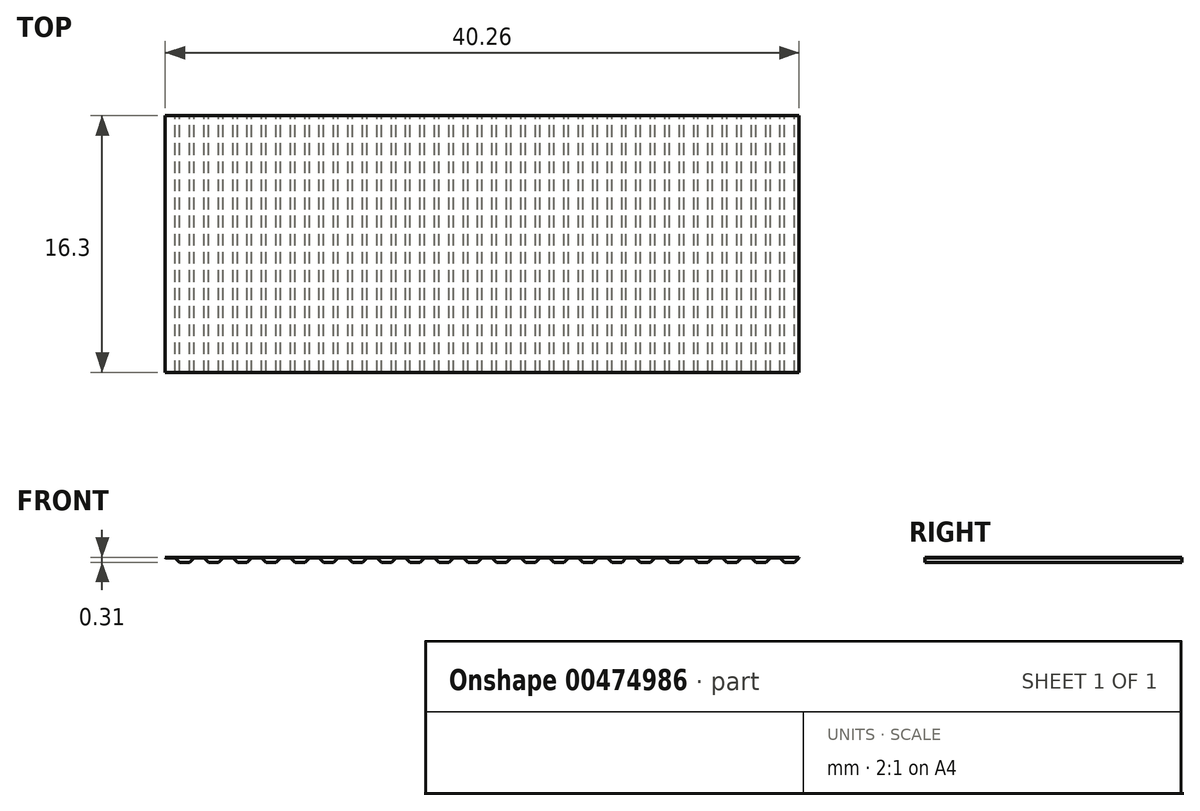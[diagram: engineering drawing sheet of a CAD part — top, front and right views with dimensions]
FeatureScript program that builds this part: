
annotation { "Feature Type Name" : "Feature", "Feature Type Description" : "" }
export const myFeature = defineFeature(function(context is Context, id is Id, definition is map)
    precondition{}
    {
        {
            var Q0;
            Q0=qCreatedBy(makeId("Front.planeOp"),FACE);
            var sketch = newSketch(context, id + "F0", { "sketchPlane" : qUnion([Q0])});
            skLineSegment(sketch, "E0", {"start": v(-5.24, 1) * mm, "end": v(-3.4, 1) * mm});
            skLineSegment(sketch, "E1", {"start": v(-5.23, 0.95) * mm, "end": v(-4.6, 0.95) * mm});
            skLineSegment(sketch, "E2", {"start": v(-4.6, 0.95) * mm, "end": v(-4.32, 0.68) * mm});
            skLineSegment(sketch, "E3", {"start": v(-4.32, 0.68) * mm, "end": v(-3.69, 0.68) * mm});
            skLineSegment(sketch, "E4", {"start": v(-3.69, 0.68) * mm, "end": v(-3.4, 0.95) * mm});
            skLineSegment(sketch, "E5", {"start": v(-5.24, 1) * mm, "end": v(-5.23, 0.95) * mm});
            skLineSegment(sketch, "E6", {"start": v(-3.4, 1) * mm, "end": v(-3.4, 0.95) * mm});
            skLineSegment(sketch, "E7", {"start": v(-3.4, 1) * mm, "end": v(-1.57, 1) * mm});
            skLineSegment(sketch, "E8", {"start": v(-3.4, 0.95) * mm, "end": v(-2.77, 0.95) * mm});
            skLineSegment(sketch, "E9", {"start": v(-2.77, 0.95) * mm, "end": v(-2.49, 0.68) * mm});
            skLineSegment(sketch, "E10", {"start": v(-2.49, 0.68) * mm, "end": v(-1.86, 0.68) * mm});
            skLineSegment(sketch, "E11", {"start": v(-1.86, 0.68) * mm, "end": v(-1.57, 0.95) * mm});
            skLineSegment(sketch, "E12", {"start": v(-1.57, 1) * mm, "end": v(-1.57, 0.95) * mm});
            skLineSegment(sketch, "E13", {"start": v(-1.58, 1) * mm, "end": v(0.26, 1) * mm});
            skLineSegment(sketch, "E14", {"start": v(-1.57, 0.95) * mm, "end": v(-0.94, 0.95) * mm});
            skLineSegment(sketch, "E15", {"start": v(-0.94, 0.95) * mm, "end": v(-0.66, 0.68) * mm});
            skLineSegment(sketch, "E16", {"start": v(-0.66, 0.68) * mm, "end": v(-0.03, 0.68) * mm});
            skLineSegment(sketch, "E17", {"start": v(-0.03, 0.68) * mm, "end": v(0.26, 0.95) * mm});
            skLineSegment(sketch, "E18", {"start": v(-1.58, 1) * mm, "end": v(-1.57, 0.95) * mm});
            skLineSegment(sketch, "E19", {"start": v(0.26, 1) * mm, "end": v(0.26, 0.95) * mm});
            skLineSegment(sketch, "E20", {"start": v(0.25, 1) * mm, "end": v(2.09, 1) * mm});
            skLineSegment(sketch, "E21", {"start": v(0.26, 0.95) * mm, "end": v(0.89, 0.95) * mm});
            skLineSegment(sketch, "E22", {"start": v(0.89, 0.95) * mm, "end": v(1.17, 0.68) * mm});
            skLineSegment(sketch, "E23", {"start": v(1.17, 0.68) * mm, "end": v(1.8, 0.68) * mm});
            skLineSegment(sketch, "E24", {"start": v(1.8, 0.68) * mm, "end": v(2.09, 0.95) * mm});
            skLineSegment(sketch, "E25", {"start": v(0.25, 1) * mm, "end": v(0.26, 0.95) * mm});
            skLineSegment(sketch, "E26", {"start": v(2.09, 1) * mm, "end": v(2.09, 0.95) * mm});
            skLineSegment(sketch, "E27", {"start": v(2.08, 1) * mm, "end": v(3.92, 1) * mm});
            skLineSegment(sketch, "E28", {"start": v(2.09, 0.95) * mm, "end": v(2.72, 0.95) * mm});
            skLineSegment(sketch, "E29", {"start": v(2.72, 0.95) * mm, "end": v(3, 0.68) * mm});
            skLineSegment(sketch, "E30", {"start": v(3, 0.68) * mm, "end": v(3.63, 0.68) * mm});
            skLineSegment(sketch, "E31", {"start": v(3.63, 0.68) * mm, "end": v(3.92, 0.95) * mm});
            skLineSegment(sketch, "E32", {"start": v(2.08, 1) * mm, "end": v(2.09, 0.95) * mm});
            skLineSegment(sketch, "E33", {"start": v(3.92, 1) * mm, "end": v(3.92, 0.95) * mm});
            skLineSegment(sketch, "E34", {"start": v(3.91, 1) * mm, "end": v(5.75, 1) * mm});
            skLineSegment(sketch, "E35", {"start": v(3.92, 0.95) * mm, "end": v(4.55, 0.95) * mm});
            skLineSegment(sketch, "E36", {"start": v(4.55, 0.95) * mm, "end": v(4.83, 0.68) * mm});
            skLineSegment(sketch, "E37", {"start": v(4.83, 0.68) * mm, "end": v(5.46, 0.68) * mm});
            skLineSegment(sketch, "E38", {"start": v(5.46, 0.68) * mm, "end": v(5.74, 0.95) * mm});
            skLineSegment(sketch, "E39", {"start": v(3.91, 1) * mm, "end": v(3.92, 0.95) * mm});
            skLineSegment(sketch, "E40", {"start": v(5.75, 1) * mm, "end": v(5.74, 0.95) * mm});
            skLineSegment(sketch, "E41", {"start": v(5.74, 1) * mm, "end": v(7.58, 1) * mm});
            skLineSegment(sketch, "E42", {"start": v(5.74, 0.95) * mm, "end": v(6.37, 0.95) * mm});
            skLineSegment(sketch, "E43", {"start": v(6.37, 0.95) * mm, "end": v(6.66, 0.68) * mm});
            skLineSegment(sketch, "E44", {"start": v(6.66, 0.68) * mm, "end": v(7.29, 0.68) * mm});
            skLineSegment(sketch, "E45", {"start": v(7.29, 0.68) * mm, "end": v(7.57, 0.95) * mm});
            skLineSegment(sketch, "E46", {"start": v(5.74, 1) * mm, "end": v(5.74, 0.95) * mm});
            skLineSegment(sketch, "E47", {"start": v(7.58, 1) * mm, "end": v(7.57, 0.95) * mm});
            skLineSegment(sketch, "E48", {"start": v(7.57, 1) * mm, "end": v(9.4, 1) * mm});
            skLineSegment(sketch, "E49", {"start": v(7.57, 0.95) * mm, "end": v(8.2, 0.95) * mm});
            skLineSegment(sketch, "E50", {"start": v(8.2, 0.95) * mm, "end": v(8.49, 0.68) * mm});
            skLineSegment(sketch, "E51", {"start": v(8.49, 0.68) * mm, "end": v(9.12, 0.68) * mm});
            skLineSegment(sketch, "E52", {"start": v(9.12, 0.68) * mm, "end": v(9.4, 0.95) * mm});
            skLineSegment(sketch, "E53", {"start": v(7.57, 1) * mm, "end": v(7.57, 0.95) * mm});
            skLineSegment(sketch, "E54", {"start": v(9.4, 1) * mm, "end": v(9.4, 0.95) * mm});
            skLineSegment(sketch, "E55", {"start": v(9.4, 1) * mm, "end": v(11.24, 1) * mm});
            skLineSegment(sketch, "E56", {"start": v(9.4, 0.95) * mm, "end": v(10.03, 0.95) * mm});
            skLineSegment(sketch, "E57", {"start": v(10.03, 0.95) * mm, "end": v(10.32, 0.68) * mm});
            skLineSegment(sketch, "E58", {"start": v(10.32, 0.68) * mm, "end": v(10.95, 0.68) * mm});
            skLineSegment(sketch, "E59", {"start": v(10.95, 0.68) * mm, "end": v(11.23, 0.95) * mm});
            skLineSegment(sketch, "E60", {"start": v(11.24, 1) * mm, "end": v(11.23, 0.95) * mm});
            skLineSegment(sketch, "E61", {"start": v(11.23, 1) * mm, "end": v(13.07, 1) * mm});
            skLineSegment(sketch, "E62", {"start": v(11.23, 0.95) * mm, "end": v(11.86, 0.95) * mm});
            skLineSegment(sketch, "E63", {"start": v(11.86, 0.95) * mm, "end": v(12.15, 0.68) * mm});
            skLineSegment(sketch, "E64", {"start": v(12.15, 0.68) * mm, "end": v(12.78, 0.68) * mm});
            skLineSegment(sketch, "E65", {"start": v(12.78, 0.68) * mm, "end": v(13.06, 0.95) * mm});
            skLineSegment(sketch, "E66", {"start": v(11.23, 1) * mm, "end": v(11.23, 0.95) * mm});
            skLineSegment(sketch, "E67", {"start": v(13.07, 1) * mm, "end": v(13.06, 0.95) * mm});
            skLineSegment(sketch, "E68", {"start": v(13.06, 1) * mm, "end": v(14.9, 1) * mm});
            skLineSegment(sketch, "E69", {"start": v(13.06, 0.95) * mm, "end": v(13.7, 0.95) * mm});
            skLineSegment(sketch, "E70", {"start": v(13.7, 0.95) * mm, "end": v(13.98, 0.68) * mm});
            skLineSegment(sketch, "E71", {"start": v(13.98, 0.68) * mm, "end": v(14.6, 0.68) * mm});
            skLineSegment(sketch, "E72", {"start": v(14.6, 0.68) * mm, "end": v(14.9, 0.95) * mm});
            skLineSegment(sketch, "E73", {"start": v(13.06, 1) * mm, "end": v(13.06, 0.95) * mm});
            skLineSegment(sketch, "E74", {"start": v(14.9, 1) * mm, "end": v(14.9, 0.95) * mm});
            skLineSegment(sketch, "E75", {"start": v(14.89, 1) * mm, "end": v(16.72, 1) * mm});
            skLineSegment(sketch, "E76", {"start": v(14.9, 0.95) * mm, "end": v(15.52, 0.95) * mm});
            skLineSegment(sketch, "E77", {"start": v(15.52, 0.95) * mm, "end": v(15.8, 0.68) * mm});
            skLineSegment(sketch, "E78", {"start": v(15.8, 0.68) * mm, "end": v(16.44, 0.68) * mm});
            skLineSegment(sketch, "E79", {"start": v(16.44, 0.68) * mm, "end": v(16.72, 0.95) * mm});
            skLineSegment(sketch, "E80", {"start": v(14.89, 1) * mm, "end": v(14.9, 0.95) * mm});
            skLineSegment(sketch, "E81", {"start": v(16.72, 1) * mm, "end": v(16.72, 0.95) * mm});
            skLineSegment(sketch, "E82", {"start": v(16.72, 1) * mm, "end": v(18.55, 1) * mm});
            skLineSegment(sketch, "E83", {"start": v(16.72, 0.95) * mm, "end": v(17.35, 0.95) * mm});
            skLineSegment(sketch, "E84", {"start": v(17.35, 0.95) * mm, "end": v(17.64, 0.68) * mm});
            skLineSegment(sketch, "E85", {"start": v(17.64, 0.68) * mm, "end": v(18.27, 0.68) * mm});
            skLineSegment(sketch, "E86", {"start": v(18.27, 0.68) * mm, "end": v(18.55, 0.95) * mm});
            skLineSegment(sketch, "E87", {"start": v(18.55, 1) * mm, "end": v(18.55, 0.95) * mm});
            skLineSegment(sketch, "E88", {"start": v(18.55, 1) * mm, "end": v(20.38, 1) * mm});
            skLineSegment(sketch, "E89", {"start": v(18.55, 0.95) * mm, "end": v(19.18, 0.95) * mm});
            skLineSegment(sketch, "E90", {"start": v(19.18, 0.95) * mm, "end": v(19.46, 0.68) * mm});
            skLineSegment(sketch, "E91", {"start": v(19.46, 0.68) * mm, "end": v(20.1, 0.68) * mm});
            skLineSegment(sketch, "E92", {"start": v(20.1, 0.68) * mm, "end": v(20.38, 0.95) * mm});
            skLineSegment(sketch, "E93", {"start": v(20.38, 1) * mm, "end": v(20.38, 0.95) * mm});
            skLineSegment(sketch, "E94", {"start": v(20.38, 1) * mm, "end": v(22.21, 1) * mm});
            skLineSegment(sketch, "E95", {"start": v(20.38, 0.95) * mm, "end": v(21, 0.95) * mm});
            skLineSegment(sketch, "E96", {"start": v(21, 0.95) * mm, "end": v(21.3, 0.68) * mm});
            skLineSegment(sketch, "E97", {"start": v(21.3, 0.68) * mm, "end": v(21.92, 0.68) * mm});
            skLineSegment(sketch, "E98", {"start": v(21.92, 0.68) * mm, "end": v(22.2, 0.95) * mm});
            skLineSegment(sketch, "E99", {"start": v(22.21, 1) * mm, "end": v(22.2, 0.95) * mm});
            skLineSegment(sketch, "E100", {"start": v(22.2, 1) * mm, "end": v(24.04, 1) * mm});
            skLineSegment(sketch, "E101", {"start": v(22.2, 0.95) * mm, "end": v(22.84, 0.95) * mm});
            skLineSegment(sketch, "E102", {"start": v(22.84, 0.95) * mm, "end": v(23.12, 0.68) * mm});
            skLineSegment(sketch, "E103", {"start": v(23.12, 0.68) * mm, "end": v(23.75, 0.68) * mm});
            skLineSegment(sketch, "E104", {"start": v(23.75, 0.68) * mm, "end": v(24.04, 0.95) * mm});
            skLineSegment(sketch, "E105", {"start": v(22.2, 1) * mm, "end": v(22.2, 0.95) * mm});
            skLineSegment(sketch, "E106", {"start": v(24.04, 1) * mm, "end": v(24.04, 0.95) * mm});
            skLineSegment(sketch, "E107", {"start": v(24.04, 1) * mm, "end": v(25.87, 1) * mm});
            skLineSegment(sketch, "E108", {"start": v(24.04, 0.95) * mm, "end": v(24.67, 0.95) * mm});
            skLineSegment(sketch, "E109", {"start": v(24.67, 0.95) * mm, "end": v(24.95, 0.68) * mm});
            skLineSegment(sketch, "E110", {"start": v(24.95, 0.68) * mm, "end": v(25.58, 0.68) * mm});
            skLineSegment(sketch, "E111", {"start": v(25.58, 0.68) * mm, "end": v(25.87, 0.95) * mm});
            skLineSegment(sketch, "E112", {"start": v(25.87, 1) * mm, "end": v(25.87, 0.95) * mm});
            skLineSegment(sketch, "E113", {"start": v(25.86, 1) * mm, "end": v(27.7, 1) * mm});
            skLineSegment(sketch, "E114", {"start": v(25.87, 0.95) * mm, "end": v(26.5, 0.95) * mm});
            skLineSegment(sketch, "E115", {"start": v(26.5, 0.95) * mm, "end": v(26.78, 0.68) * mm});
            skLineSegment(sketch, "E116", {"start": v(26.78, 0.68) * mm, "end": v(27.41, 0.68) * mm});
            skLineSegment(sketch, "E117", {"start": v(27.41, 0.68) * mm, "end": v(27.7, 0.95) * mm});
            skLineSegment(sketch, "E118", {"start": v(25.86, 1) * mm, "end": v(25.87, 0.95) * mm});
            skLineSegment(sketch, "E119", {"start": v(27.7, 1) * mm, "end": v(27.7, 0.95) * mm});
            skLineSegment(sketch, "E120", {"start": v(27.7, 1) * mm, "end": v(29.53, 1) * mm});
            skLineSegment(sketch, "E121", {"start": v(27.7, 0.95) * mm, "end": v(28.33, 0.95) * mm});
            skLineSegment(sketch, "E122", {"start": v(28.33, 0.95) * mm, "end": v(28.61, 0.68) * mm});
            skLineSegment(sketch, "E123", {"start": v(28.61, 0.68) * mm, "end": v(29.24, 0.68) * mm});
            skLineSegment(sketch, "E124", {"start": v(29.24, 0.68) * mm, "end": v(29.53, 0.95) * mm});
            skLineSegment(sketch, "E125", {"start": v(29.53, 1) * mm, "end": v(29.53, 0.95) * mm});
            skLineSegment(sketch, "E126", {"start": v(29.52, 1) * mm, "end": v(31.36, 1) * mm});
            skLineSegment(sketch, "E127", {"start": v(29.53, 0.95) * mm, "end": v(30.16, 0.95) * mm});
            skLineSegment(sketch, "E128", {"start": v(30.16, 0.95) * mm, "end": v(30.44, 0.68) * mm});
            skLineSegment(sketch, "E129", {"start": v(30.44, 0.68) * mm, "end": v(31.07, 0.68) * mm});
            skLineSegment(sketch, "E130", {"start": v(31.07, 0.68) * mm, "end": v(31.36, 0.95) * mm});
            skLineSegment(sketch, "E131", {"start": v(29.52, 1) * mm, "end": v(29.53, 0.95) * mm});
            skLineSegment(sketch, "E132", {"start": v(31.36, 1) * mm, "end": v(31.36, 0.95) * mm});
            skLineSegment(sketch, "E133", {"start": v(31.35, 1) * mm, "end": v(33.19, 1) * mm});
            skLineSegment(sketch, "E134", {"start": v(31.36, 0.95) * mm, "end": v(31.99, 0.95) * mm});
            skLineSegment(sketch, "E135", {"start": v(31.99, 0.95) * mm, "end": v(32.27, 0.68) * mm});
            skLineSegment(sketch, "E136", {"start": v(32.27, 0.68) * mm, "end": v(32.9, 0.68) * mm});
            skLineSegment(sketch, "E137", {"start": v(32.9, 0.68) * mm, "end": v(33.19, 0.95) * mm});
            skLineSegment(sketch, "E138", {"start": v(31.35, 1) * mm, "end": v(31.36, 0.95) * mm});
            skLineSegment(sketch, "E139", {"start": v(33.19, 1) * mm, "end": v(33.19, 0.95) * mm});
            skLineSegment(sketch, "E140", {"start": v(33.18, 1) * mm, "end": v(35.02, 1) * mm});
            skLineSegment(sketch, "E141", {"start": v(33.19, 0.95) * mm, "end": v(33.82, 0.95) * mm});
            skLineSegment(sketch, "E142", {"start": v(33.82, 0.95) * mm, "end": v(34.1, 0.68) * mm});
            skLineSegment(sketch, "E143", {"start": v(34.1, 0.68) * mm, "end": v(34.73, 0.68) * mm});
            skLineSegment(sketch, "E144", {"start": v(34.73, 0.68) * mm, "end": v(35.01, 0.95) * mm});
            skLineSegment(sketch, "E145", {"start": v(33.18, 1) * mm, "end": v(33.19, 0.95) * mm});
            skLineSegment(sketch, "E146", {"start": v(35.02, 1) * mm, "end": v(35.01, 0.95) * mm});
            skSolve(sketch);
        }
        {
            var Q0;
            Q0 = qSketchRegion(id + "F0", true);
            extrude(context, id + "F1", {"entities" : qUnion([Q0]), "depth" : 16.3 * mm});
        }
    });
